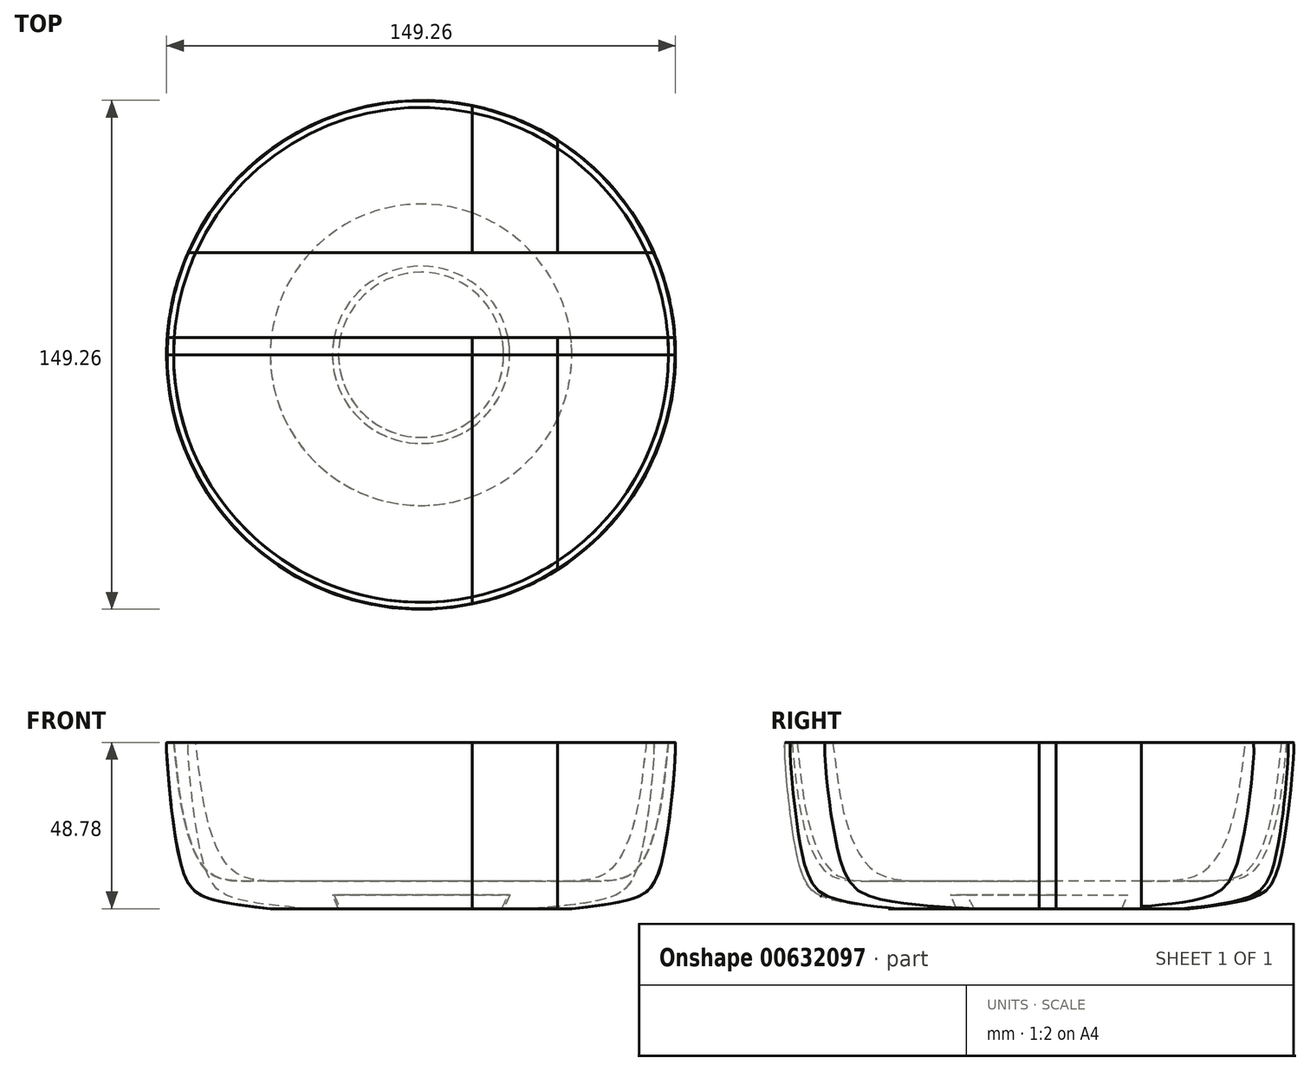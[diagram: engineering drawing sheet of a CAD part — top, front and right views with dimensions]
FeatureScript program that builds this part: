
annotation { "Feature Type Name" : "Feature", "Feature Type Description" : "" }
export const myFeature = defineFeature(function(context is Context, id is Id, definition is map)
    precondition{}
    {
        {
            var Q0;
            Q0=qCreatedBy(makeId("Top.planeOp"),FACE);
            var sketch = newSketch(context, id + "F0", { "sketchPlane" : qUnion([Q0])});
            skLineSegment(sketch, "E0.bottom", {"start": v(0, 0) * mm, "end": v(90, 0) * mm});
            skLineSegment(sketch, "E0.top", {"start": v(0, 25) * mm, "end": v(90, 25) * mm});
            skLineSegment(sketch, "E0.left", {"start": v(0, 0) * mm, "end": v(0, 25) * mm});
            skLineSegment(sketch, "E1.bottom", {"start": v(90, 25) * mm, "end": v(115, 25) * mm});
            skLineSegment(sketch, "E1.top", {"start": v(100, 0) * mm, "end": v(115, 0) * mm});
            skLineSegment(sketch, "E2.bottom", {"start": v(115, 25) * mm, "end": v(160, 25) * mm});
            skLineSegment(sketch, "E2.top", {"start": v(125, 0) * mm, "end": v(160, 0) * mm});
            skLineSegment(sketch, "E2.right", {"start": v(160, 25) * mm, "end": v(160, 0) * mm});
            skLineSegment(sketch, "E3.top", {"start": v(0, 70) * mm, "end": v(90, 70) * mm});
            skLineSegment(sketch, "E3.left", {"start": v(0, 25) * mm, "end": v(0, 70) * mm});
            skLineSegment(sketch, "E3.right", {"start": v(90, 25) * mm, "end": v(90, 70) * mm});
            skLineSegment(sketch, "E4.bottom", {"start": v(90, 70) * mm, "end": v(115, 70) * mm});
            skLineSegment(sketch, "E4.left", {"start": v(90, 70) * mm, "end": v(90, 25) * mm});
            skLineSegment(sketch, "E4.right", {"start": v(115, 70) * mm, "end": v(115, 25) * mm});
            skLineSegment(sketch, "E5.bottom", {"start": v(115, 70) * mm, "end": v(160, 70) * mm});
            skLineSegment(sketch, "E5.right", {"start": v(160, 70) * mm, "end": v(160, 25) * mm});
            skLineSegment(sketch, "E6.top", {"start": v(0, -80) * mm, "end": v(90, -80) * mm});
            skLineSegment(sketch, "E6.left", {"start": v(0, 0) * mm, "end": v(0, -80) * mm});
            skLineSegment(sketch, "E6.right", {"start": v(90, 0) * mm, "end": v(90, -80) * mm});
            skLineSegment(sketch, "E7.bottom", {"start": v(90, 0) * mm, "end": v(115, 0) * mm});
            skLineSegment(sketch, "E7.top", {"start": v(90, -80) * mm, "end": v(115, -80) * mm});
            skLineSegment(sketch, "E7.right", {"start": v(115, 0) * mm, "end": v(115, -80) * mm});
            skLineSegment(sketch, "E8.bottom", {"start": v(115, 0) * mm, "end": v(160, 0) * mm});
            skLineSegment(sketch, "E8.top", {"start": v(115, -80) * mm, "end": v(160, -80) * mm});
            skLineSegment(sketch, "E8.right", {"start": v(160, 0) * mm, "end": v(160, -80) * mm});
            skLineSegment(sketch, "E9", {"start": v(0, -5) * mm, "end": v(160, -5) * mm});
            skLineSegment(sketch, "E10", {"start": v(85, -89.76) * mm, "end": v(85, 111.9) * mm, "construction": true});
            skSolve(sketch);
        }
        {
            var Q0;
            Q0=makeQuery(id+"F0.imprint","IMPRINT",FACE,{"disambiguationData":[TD([[makeQuery(id+"F0.imprint","IMPRINT",EDGE,{"derivedFrom":sQuery(id+"F0.wireOp",EDGE,"E0.top")}),1.0]])]});
            extrude(context, id + "F1", {"entities" : qUnion([Q0]), "depth" : 50 * mm, "offsetDistance" : 25 * mm});
        }
        {
            var Q0;
            Q0=makeQuery(id+"F0.imprint","IMPRINT",FACE,{"disambiguationData":[TD([[makeQuery(id+"F0.imprint","IMPRINT",EDGE,{"derivedFrom":sQuery(id+"F0.wireOp",EDGE,"E4.bottom")}),-1.0]])]});
            extrude(context, id + "F2", {"entities" : qUnion([Q0]), "depth" : 50 * mm, "offsetDistance" : 25 * mm});
        }
        {
            var Q0;
            Q0=makeQuery(id+"F0.imprint","IMPRINT",FACE,{"disambiguationData":[TD([[makeQuery(id+"F0.imprint","IMPRINT",EDGE,{"derivedFrom":sQuery(id+"F0.wireOp",EDGE,"E5.bottom")}),-1.0]])]});
            extrude(context, id + "F3", {"entities" : qUnion([Q0]), "depth" : 50 * mm, "offsetDistance" : 25 * mm});
        }
        {
            var Q0;
            Q0=makeQuery(id+"F0.imprint","IMPRINT",FACE,{"disambiguationData":[TD([[makeQuery(id+"F0.imprint","IMPRINT",EDGE,{"derivedFrom":sQuery(id+"F0.wireOp",EDGE,"E0.left")}),-1.0]])]});
            extrude(context, id + "F4", {"entities" : qUnion([Q0]), "depth" : 50 * mm, "offsetDistance" : 25 * mm});
        }
        {
            var Q0;
            Q0=makeQuery(id+"F0.imprint","IMPRINT",FACE,{"disambiguationData":[TD([[makeQuery(id+"F0.imprint","IMPRINT",EDGE,{"derivedFrom":sQuery(id+"F0.wireOp",EDGE,"E1.left")}),1.0]])]});
            var Q1;
            {var subQ0=sQuery(id+"F0.wireOp",EDGE,"E0.bottom");Q1=makeQuery(id+"F0.imprint","IMPRINT",FACE,{"disambiguationData":[TD([[makeQuery(id+"F0.imprint","IMPRINT",EDGE,{"derivedFrom":subQ0}),-1.0]])]});}
            var Q2;
            {var subQ0=sQuery(id+"F0.wireOp",EDGE,"E8.bottom");Q2=makeQuery(id+"F0.imprint","IMPRINT",FACE,{"disambiguationData":[TD([[makeQuery(id+"F0.imprint","IMPRINT",EDGE,{"derivedFrom":subQ0}),-1.0]])]});}
            var Q3;
            {var subQ0=sQuery(id+"F0.wireOp",EDGE,"E6.top");Q3=makeQuery(id+"F0.imprint","IMPRINT",FACE,{"disambiguationData":[TD([[makeQuery(id+"F0.imprint","IMPRINT",EDGE,{"derivedFrom":subQ0}),1.0]])]});}
            var Q4;
            {var subQ0=sQuery(id+"F0.wireOp",EDGE,"E8.top");Q4=makeQuery(id+"F0.imprint","IMPRINT",FACE,{"disambiguationData":[TD([[makeQuery(id+"F0.imprint","IMPRINT",EDGE,{"derivedFrom":subQ0}),1.0]])]});}
            extrude(context, id + "F5", {"entities" : qUnion([Q0, Q1, Q2, Q3, Q4]), "depth" : 50 * mm, "offsetDistance" : 25 * mm});
        }
        {
            var Q0;
            {var subQ0=sQuery(id+"F0.wireOp",EDGE,"E7.bottom");Q0=makeQuery(id+"F0.imprint","IMPRINT",FACE,{"disambiguationData":[TD([[makeQuery(id+"F0.imprint","IMPRINT",EDGE,{"derivedFrom":subQ0}),-1.0]])]});}
            var Q1;
            {var subQ0=sQuery(id+"F0.wireOp",EDGE,"E7.top");Q1=makeQuery(id+"F0.imprint","IMPRINT",FACE,{"disambiguationData":[TD([[makeQuery(id+"F0.imprint","IMPRINT",EDGE,{"derivedFrom":subQ0}),1.0]])]});}
            extrude(context, id + "F6", {"entities" : qUnion([Q0, Q1]), "depth" : 50 * mm, "offsetDistance" : 25 * mm});
        }
        {
            var Q0;
            {var subQ0=sQuery(id+"F0.wireOp",EDGE,"E0.bottom");Q0=makeQuery(id+"F0.imprint","IMPRINT",FACE,{"disambiguationData":[TD([[makeQuery(id+"F0.imprint","IMPRINT",EDGE,{"derivedFrom":subQ0}),-1.0]])]});}
            extrude(context, id + "F7", {"entities" : qUnion([Q0]), "depth" : 50 * mm, "offsetDistance" : 25 * mm});
        }
        {
            var Q0;
            {var subQ0=sQuery(id+"F0.wireOp",EDGE,"E7.bottom");Q0=makeQuery(id+"F0.imprint","IMPRINT",FACE,{"disambiguationData":[TD([[makeQuery(id+"F0.imprint","IMPRINT",EDGE,{"derivedFrom":subQ0}),-1.0]])]});}
            extrude(context, id + "F8", {"entities" : qUnion([Q0]), "depth" : 50 * mm, "offsetDistance" : 25 * mm});
        }
        {
            var Q0;
            {var subQ0=sQuery(id+"F0.wireOp",EDGE,"E8.bottom");Q0=makeQuery(id+"F0.imprint","IMPRINT",FACE,{"disambiguationData":[TD([[makeQuery(id+"F0.imprint","IMPRINT",EDGE,{"derivedFrom":subQ0}),-1.0]])]});}
            extrude(context, id + "F9", {"entities" : qUnion([Q0]), "depth" : 50 * mm, "offsetDistance" : 25 * mm});
        }
        {
            var Q0;
            {var subQ0=sQuery(id+"F0.wireOp",EDGE,"E6.top");Q0=makeQuery(id+"F0.imprint","IMPRINT",FACE,{"disambiguationData":[TD([[makeQuery(id+"F0.imprint","IMPRINT",EDGE,{"derivedFrom":subQ0}),1.0]])]});}
            extrude(context, id + "F10", {"entities" : qUnion([Q0]), "depth" : 50 * mm, "offsetDistance" : 25 * mm});
        }
        {
            var Q0;
            {var subQ0=sQuery(id+"F0.wireOp",EDGE,"E7.top");Q0=makeQuery(id+"F0.imprint","IMPRINT",FACE,{"disambiguationData":[TD([[makeQuery(id+"F0.imprint","IMPRINT",EDGE,{"derivedFrom":subQ0}),1.0]])]});}
            extrude(context, id + "F11", {"entities" : qUnion([Q0]), "depth" : 50 * mm, "offsetDistance" : 25 * mm});
        }
        {
            var Q0;
            {var subQ0=sQuery(id+"F0.wireOp",EDGE,"E8.top");Q0=makeQuery(id+"F0.imprint","IMPRINT",FACE,{"disambiguationData":[TD([[makeQuery(id+"F0.imprint","IMPRINT",EDGE,{"derivedFrom":subQ0}),1.0]])]});}
            extrude(context, id + "F12", {"entities" : qUnion([Q0]), "depth" : 50 * mm, "offsetDistance" : 25 * mm});
        }
        {
            var Q0;
            Q0=makeQuery(id+"F7.opExtrude","SWEPT_FACE",FACE,{"disambiguationData":[OSD([sQuery(id+"F0.wireOp",EDGE,"E9")])]});
            var sketch = newSketch(context, id + "F13", { "sketchPlane" : qUnion([Q0])});
            skLineSegment(sketch, "E11", {"start": v(75, 72.12) * mm, "end": v(75, -27.18) * mm, "construction": true});
            skLineSegment(sketch, "E12", {"start": v(75, 4) * mm, "end": v(101, 4) * mm});
            skLineSegment(sketch, "E13", {"start": v(101, 4) * mm, "end": v(99.2, 0) * mm});
            skLineSegment(sketch, "E14", {"start": v(99.2, 0) * mm, "end": v(119.2, 0) * mm});
            skLineSegment(sketch, "E15", {"start": v(75, 8.1) * mm, "end": v(120, 8.1) * mm});
            skFitSpline(sketch, "E16", {"points": [v(119.2, 0) * mm, v(137.89, 3.26) * mm, v(145.42, 13.09) * mm, v(149.54, 48.76) * mm, v(149.46, 48.76) * mm], "startDerivative": vector(68.66, 7.54) * mm, "endDerivative": vector(-4.23, -2.58) * mm});
            skFitSpline(sketch, "E17", {"points": [v(120, 8.1) * mm, v(137.42, 10.74) * mm, v(144.55, 26.48) * mm, v(147.56, 48.76) * mm], "startDerivative": vector(87.08, 0) * mm, "endDerivative": vector(7.06, 60.03) * mm});
            skLineSegment(sketch, "E18", {"start": v(147.56, 48.76) * mm, "end": v(149.46, 48.76) * mm});
            skLineSegment(sketch, "E19", {"start": v(75, 8.1) * mm, "end": v(75, 4) * mm});
            skSolve(sketch);
        }
        {
            var Q0;
            {var subQ0=sQuery(id+"F13.wireOp",EDGE,"E19");Q0=makeQuery(id+"F13.imprint","IMPRINT",FACE,{"disambiguationData":[TD([[makeQuery(id+"F13.imprint","IMPRINT",EDGE,{"derivedFrom":subQ0}),1.0]])]});}
            var Q1;
            {var subQ3=sQuery(id+"F13.wireOp",EDGE,"E16");Q1=makeQuery(id+"F13.imprint","IMPRINT",FACE,{"disambiguationData":[TD([[makeQuery(id+"F13.imprint","IMPRINT",EDGE,{"derivedFrom":subQ3}),1.0]])]});}
            var Q2;
            {var subQ0=sQuery(id+"F13.wireOp",EDGE,"E14");var subQ1=sQuery(id+"F13.wireOp",EDGE,"E13");var subQ2=sQuery(id+"F0.wireOp",EDGE,"E9");var subQ3=makeQuery(id+"F13.imprint","INTERSECT",VERTEX,{"derivedFrom":[makeQuery(id+"F7.opExtrude","CAP_EDGE",EDGE,{"disambiguationData":[OSD([subQ2])],"isStart":true}),subQ1,subQ0]});Q2=makeQuery(id+"F13.imprint","IMPRINT",FACE,{"disambiguationData":[TD([[makeQuery(id+"F13.imprint","IMPRINT",EDGE,{"disambiguationData":[TD([[subQ3,1.0]])],"derivedFrom":subQ1}),1.0]])]});}
            var Q3;
            Q3=sQuery(id+"F13.wireOp",EDGE,"E11");
            revolve(context, id + "F14", {"operationType" : NewBodyOperationType.INTERSECT, "entities" : qUnion([Q0, Q1, Q2]), "axis" : qUnion([Q3]), "revolveType" : RevolveType.FULL, "oppositeDirection" : true});
        }
    });
